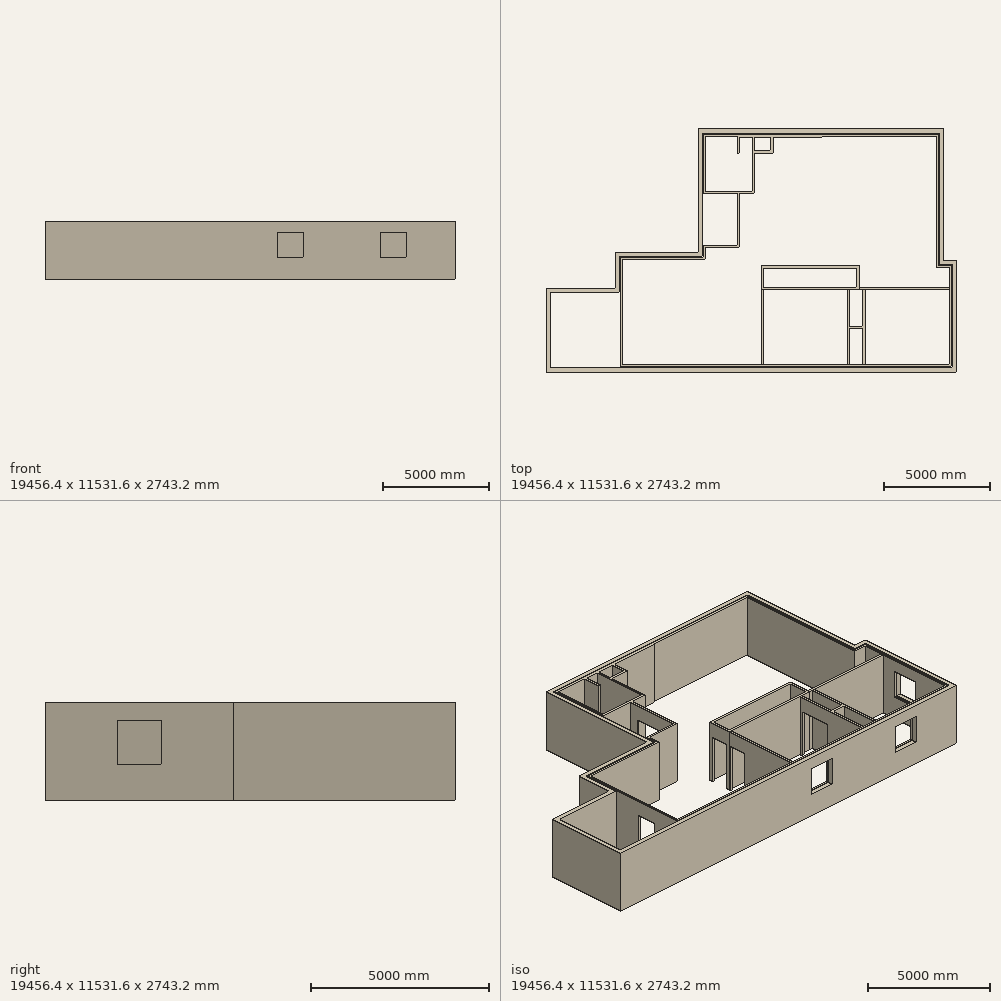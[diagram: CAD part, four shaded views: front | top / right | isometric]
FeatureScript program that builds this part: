
annotation { "Feature Type Name" : "Feature", "Feature Type Description" : "" }
export const myFeature = defineFeature(function(context is Context, id is Id, definition is map)
    precondition{}
    {
        {
            var Q0;
            Q0=qCreatedBy(makeId("Top.planeOp"),FACE);
            var sketch = newSketch(context, id + "F0", { "sketchPlane" : qUnion([Q0])});
            skLineSegment(sketch, "E0.bottom", {"start": v(0, 0) * mm, "end": v(19050, 0) * mm});
            skLineSegment(sketch, "E0.top", {"start": v(7213.6, 11125.2) * mm, "end": v(18440.4, 11125.2) * mm});
            skLineSegment(sketch, "E0.left", {"start": v(0, 0) * mm, "end": v(0, 3556) * mm});
            skLineSegment(sketch, "E0.right", {"start": v(19050, 0) * mm, "end": v(19050, 4876.8) * mm});
            skLineSegment(sketch, "E1", {"start": v(18440.4, 11125.2) * mm, "end": v(18440.4, 4876.8) * mm});
            skLineSegment(sketch, "E2", {"start": v(18440.4, 4876.8) * mm, "end": v(19050, 4876.8) * mm});
            skLineSegment(sketch, "E3", {"start": v(7213.6, 11125.2) * mm, "end": v(7213.6, 5283.2) * mm});
            skLineSegment(sketch, "E4", {"start": v(7213.6, 5283.2) * mm, "end": v(3276.6, 5283.2) * mm});
            skLineSegment(sketch, "E5", {"start": v(3276.6, 5283.2) * mm, "end": v(3276.6, 3556) * mm});
            skLineSegment(sketch, "E6", {"start": v(3276.6, 3556) * mm, "end": v(0, 3556) * mm});
            skLineSegment(sketch, "E7.bottom", {"start": v(9994.9, 4826) * mm, "end": v(14630.4, 4826) * mm, "construction": true});
            skLineSegment(sketch, "E7.top", {"start": v(9994.9, 3708.4) * mm, "end": v(14630.4, 3708.4) * mm, "construction": true});
            skLineSegment(sketch, "E7.left", {"start": v(9994.9, 4826) * mm, "end": v(9994.9, 3708.4) * mm, "construction": true});
            skLineSegment(sketch, "E7.right", {"start": v(14630.4, 4826) * mm, "end": v(14630.4, 3708.4) * mm, "construction": true});
            skPoint(sketch, "E8", {"position": v(16916.4, 0) * mm});
            skPoint(sketch, "E9", {"position": v(15697.2, 0) * mm});
            skPoint(sketch, "E10", {"position": v(12039.6, 0) * mm});
            skPoint(sketch, "E11", {"position": v(10820.4, 0) * mm});
            skPoint(sketch, "E12", {"position": v(12039.6, 11125.2) * mm});
            skPoint(sketch, "E13", {"position": v(10820.4, 11125.2) * mm});
            skPoint(sketch, "E14", {"position": v(19050, 1828.8) * mm});
            skPoint(sketch, "E15", {"position": v(19050, 3048) * mm});
            skLineSegment(sketch, "E16.0", {"start": v(7010.4, 11328.4) * mm, "end": v(18643.6, 11328.4) * mm});
            skLineSegment(sketch, "E17.0", {"start": v(18643.6, 11328.4) * mm, "end": v(18643.6, 5080) * mm});
            skLineSegment(sketch, "E18.0", {"start": v(18643.6, 5080) * mm, "end": v(19253.2, 5080) * mm});
            skLineSegment(sketch, "E19.0", {"start": v(19253.2, -203.2) * mm, "end": v(19253.2, 5080) * mm});
            skLineSegment(sketch, "E20.0", {"start": v(-203.2, -203.2) * mm, "end": v(19253.2, -203.2) * mm});
            skLineSegment(sketch, "E21.0", {"start": v(-203.2, -203.2) * mm, "end": v(-203.2, 3759.2) * mm});
            skLineSegment(sketch, "E22.0", {"start": v(3073.4, 3759.2) * mm, "end": v(-203.2, 3759.2) * mm});
            skLineSegment(sketch, "E23.0", {"start": v(3073.4, 5486.4) * mm, "end": v(3073.4, 3759.2) * mm});
            skLineSegment(sketch, "E24.0", {"start": v(7010.4, 5486.4) * mm, "end": v(3073.4, 5486.4) * mm});
            skLineSegment(sketch, "E25.0", {"start": v(7010.4, 11328.4) * mm, "end": v(7010.4, 5486.4) * mm});
            skPoint(sketch, "E26", {"position": v(8585.2, 11010.9) * mm});
            skPoint(sketch, "E27", {"position": v(9309.1, 10909.3) * mm});
            skPoint(sketch, "E28", {"position": v(8534.4, 10604.5) * mm});
            skSolve(sketch);
        }
        {
            var Q0;
            Q0=qCreatedBy(makeId("Top.planeOp"),FACE);
            var sketch = newSketch(context, id + "F1", { "sketchPlane" : qUnion([Q0])});
            skLineSegment(sketch, "E29", {"start": v(10972.8, 12242.8) * mm, "end": v(10795, 11328.4) * mm});
            skLineSegment(sketch, "E30", {"start": v(10795, 11328.4) * mm, "end": v(12065, 11328.4) * mm});
            skLineSegment(sketch, "E31", {"start": v(12065, 11328.4) * mm, "end": v(11887.2, 12242.8) * mm});
            skLineSegment(sketch, "E32", {"start": v(11887.2, 12242.8) * mm, "end": v(10972.8, 12242.8) * mm});
            skLineSegment(sketch, "E33", {"start": v(10820.4, 11125.2) * mm, "end": v(12039.6, 11125.2) * mm, "construction": true});
            skLineSegment(sketch, "E34", {"start": v(11430, 12242.8) * mm, "end": v(11430, 11125.2) * mm, "construction": true});
            skLineSegment(sketch, "E35", {"start": v(19050, 1828.8) * mm, "end": v(19050, 3048) * mm, "construction": true});
            skLineSegment(sketch, "E36", {"start": v(19253.2, 3073.4) * mm, "end": v(19253.2, 1803.4) * mm});
            skLineSegment(sketch, "E37", {"start": v(19253.2, 1803.4) * mm, "end": v(20167.6, 1981.2) * mm});
            skLineSegment(sketch, "E38", {"start": v(20167.6, 1981.2) * mm, "end": v(20167.6, 2895.6) * mm});
            skLineSegment(sketch, "E39", {"start": v(20167.6, 2895.6) * mm, "end": v(19253.2, 3073.4) * mm});
            skLineSegment(sketch, "E40", {"start": v(19050, 2438.4) * mm, "end": v(19253.2, 2438.4) * mm, "construction": true});
            skLineSegment(sketch, "E41", {"start": v(15697.2, 0) * mm, "end": v(16916.4, 0) * mm, "construction": true});
            skLineSegment(sketch, "E42", {"start": v(16306.8, 0) * mm, "end": v(16306.8, -203.2) * mm, "construction": true});
            skLineSegment(sketch, "E43", {"start": v(15671.8, -203.2) * mm, "end": v(16941.8, -203.2) * mm});
            skLineSegment(sketch, "E44", {"start": v(16941.8, -203.2) * mm, "end": v(16764, -1117.6) * mm});
            skLineSegment(sketch, "E45", {"start": v(16764, -1117.6) * mm, "end": v(15849.6, -1117.6) * mm});
            skLineSegment(sketch, "E46", {"start": v(15849.6, -1117.6) * mm, "end": v(15671.8, -203.2) * mm});
            skLineSegment(sketch, "E47", {"start": v(10820.4, 0) * mm, "end": v(12039.6, 0) * mm, "construction": true});
            skLineSegment(sketch, "E48", {"start": v(10795, -203.2) * mm, "end": v(10972.8, -1117.6) * mm});
            skLineSegment(sketch, "E49", {"start": v(10972.8, -1117.6) * mm, "end": v(11887.2, -1117.6) * mm});
            skLineSegment(sketch, "E50", {"start": v(11887.2, -1117.6) * mm, "end": v(12065, -203.2) * mm});
            skLineSegment(sketch, "E51", {"start": v(12065, -203.2) * mm, "end": v(10795, -203.2) * mm});
            skLineSegment(sketch, "E52", {"start": v(11430, 0) * mm, "end": v(11430, -203.2) * mm, "construction": true});
            skSolve(sketch);
        }
        {
            var Q0;
            Q0=makeQuery(id+"F0.imprint","IMPRINT",FACE,{"disambiguationData":[TD([[makeQuery(id+"F0.imprint","IMPRINT",EDGE,{"derivedFrom":sQuery(id+"F0.wireOp",EDGE,"E0.bottom")}),-1.0]])]});
            extrude(context, id + "F2", {"entities" : qUnion([Q0]), "depth" : 2743.2 * mm});
        }
        {
            var Q0;
            Q0=qCreatedBy(makeId("Top.planeOp"),FACE);
            var sketch = newSketch(context, id + "F3", { "sketchPlane" : qUnion([Q0])});
            skLineSegment(sketch, "E53.bottom", {"start": v(10096.5, 4724.4) * mm, "end": v(14528.8, 4724.4) * mm});
            skLineSegment(sketch, "E53.top", {"start": v(10096.5, 3810) * mm, "end": v(14528.8, 3810) * mm});
            skLineSegment(sketch, "E53.left", {"start": v(10096.5, 4724.4) * mm, "end": v(10096.5, 3810) * mm});
            skLineSegment(sketch, "E53.right", {"start": v(14528.8, 4724.4) * mm, "end": v(14528.8, 3810) * mm});
            skLineSegment(sketch, "E54.bottom", {"start": v(9982.2, 4838.7) * mm, "end": v(14643.1, 4838.7) * mm});
            skLineSegment(sketch, "E54.top", {"start": v(9982.2, 3695.7) * mm, "end": v(14643.1, 3695.7) * mm});
            skLineSegment(sketch, "E54.left", {"start": v(9982.2, 4838.7) * mm, "end": v(9982.2, 3695.7) * mm});
            skLineSegment(sketch, "E54.right", {"start": v(14643.1, 4838.7) * mm, "end": v(14643.1, 3695.7) * mm});
            skSolve(sketch);
        }
        {
            var Q0;
            Q0 = qSketchRegion(id + "F3", true);
            extrude(context, id + "F4", {"entities" : qUnion([Q0]), "depth" : 2743.2 * mm});
        }
        {
            var Q0;
            Q0=qCreatedBy(makeId("Top.planeOp"),FACE);
            var sketch = newSketch(context, id + "F5", { "sketchPlane" : qUnion([Q0])});
            skLineSegment(sketch, "E55", {"start": v(3314.7, 5245.1) * mm, "end": v(3314.7, 38.1) * mm});
            skLineSegment(sketch, "E56", {"start": v(3314.7, 38.1) * mm, "end": v(19011.9, 38.1) * mm});
            skLineSegment(sketch, "E57", {"start": v(19011.9, 38.1) * mm, "end": v(19011.9, 4838.7) * mm});
            skLineSegment(sketch, "E58", {"start": v(19011.9, 4838.7) * mm, "end": v(18402.3, 4838.7) * mm});
            skLineSegment(sketch, "E59", {"start": v(18402.3, 4838.7) * mm, "end": v(18402.3, 11087.1) * mm});
            skLineSegment(sketch, "E60", {"start": v(18402.3, 11087.1) * mm, "end": v(7251.7, 11087.1) * mm});
            skLineSegment(sketch, "E61", {"start": v(7251.7, 11087.1) * mm, "end": v(7251.7, 8280.4) * mm});
            skLineSegment(sketch, "E62", {"start": v(7251.7, 8280.4) * mm, "end": v(8839.2, 8280.4) * mm});
            skLineSegment(sketch, "E63", {"start": v(8839.2, 8280.4) * mm, "end": v(8839.2, 5791.2) * mm});
            skLineSegment(sketch, "E64", {"start": v(8839.2, 5791.2) * mm, "end": v(7251.7, 5791.2) * mm});
            skLineSegment(sketch, "E65", {"start": v(7251.7, 5791.2) * mm, "end": v(7251.7, 5245.1) * mm});
            skLineSegment(sketch, "E66", {"start": v(7251.7, 5245.1) * mm, "end": v(3314.7, 5245.1) * mm});
            skLineSegment(sketch, "E67.0", {"start": v(18300.7, 10985.5) * mm, "end": v(7353.3, 10985.5) * mm});
            skLineSegment(sketch, "E67.1", {"start": v(7353.3, 5689.6) * mm, "end": v(7353.3, 5143.5) * mm});
            skLineSegment(sketch, "E67.2", {"start": v(8940.8, 5689.6) * mm, "end": v(7353.3, 5689.6) * mm});
            skLineSegment(sketch, "E67.3", {"start": v(8940.8, 8382) * mm, "end": v(8940.8, 5689.6) * mm});
            skLineSegment(sketch, "E67.4", {"start": v(7353.3, 8382) * mm, "end": v(8940.8, 8382) * mm});
            skLineSegment(sketch, "E67.5", {"start": v(7353.3, 5143.5) * mm, "end": v(3416.3, 5143.5) * mm});
            skLineSegment(sketch, "E67.6", {"start": v(7353.3, 10985.5) * mm, "end": v(7353.3, 8382) * mm});
            skLineSegment(sketch, "E67.7", {"start": v(3416.3, 5143.5) * mm, "end": v(3416.3, 139.7) * mm});
            skLineSegment(sketch, "E67.8", {"start": v(3416.3, 139.7) * mm, "end": v(18910.3, 139.7) * mm});
            skLineSegment(sketch, "E67.9", {"start": v(18910.3, 139.7) * mm, "end": v(18910.3, 4737.1) * mm});
            skLineSegment(sketch, "E67.10", {"start": v(18910.3, 4737.1) * mm, "end": v(18300.7, 4737.1) * mm});
            skLineSegment(sketch, "E67.11", {"start": v(18300.7, 4737.1) * mm, "end": v(18300.7, 10985.5) * mm});
            skSolve(sketch);
        }
        {
            var Q0;
            Q0 = qSketchRegion(id + "F5", true);
            extrude(context, id + "F6", {"entities" : qUnion([Q0]), "depth" : 2743.2 * mm});
        }
        {
            var Q0;
            Q0=qCreatedBy(makeId("Top.planeOp"),FACE);
            var sketch = newSketch(context, id + "F7", { "sketchPlane" : qUnion([Q0])});
            skLineSegment(sketch, "E68", {"start": v(8940.8, 8382) * mm, "end": v(9569.45, 8382) * mm});
            skLineSegment(sketch, "E69", {"start": v(9569.45, 8382) * mm, "end": v(9569.45, 10934.7) * mm});
            skLineSegment(sketch, "E70", {"start": v(9683.75, 10934.7) * mm, "end": v(9683.75, 10299.7) * mm});
            skLineSegment(sketch, "E71", {"start": v(9683.75, 8280.4) * mm, "end": v(8940.8, 8280.4) * mm});
            skLineSegment(sketch, "E72", {"start": v(8940.8, 8280.4) * mm, "end": v(8940.8, 8382) * mm});
            skLineSegment(sketch, "E73.bottom", {"start": v(8845.55, 10934.7) * mm, "end": v(8959.85, 10934.7) * mm});
            skLineSegment(sketch, "E73.top", {"start": v(8845.55, 10172.7) * mm, "end": v(8959.85, 10172.7) * mm});
            skLineSegment(sketch, "E73.left", {"start": v(8845.55, 10934.7) * mm, "end": v(8845.55, 10172.7) * mm});
            skLineSegment(sketch, "E73.right", {"start": v(8959.85, 10934.7) * mm, "end": v(8959.85, 10172.7) * mm});
            skLineSegment(sketch, "E74", {"start": v(10560.05, 10934.7) * mm, "end": v(10560.05, 10185.4) * mm});
            skLineSegment(sketch, "E75", {"start": v(10560.05, 10185.4) * mm, "end": v(9683.75, 10185.4) * mm});
            skLineSegment(sketch, "E76", {"start": v(9683.75, 10299.7) * mm, "end": v(10445.75, 10299.7) * mm});
            skLineSegment(sketch, "E77", {"start": v(10445.75, 10299.7) * mm, "end": v(10445.75, 10934.7) * mm});
            skLineSegment(sketch, "E78.bottom", {"start": v(8845.55, 10985.5) * mm, "end": v(12903.2, 10985.5) * mm});
            skLineSegment(sketch, "E78.top", {"start": v(8845.55, 10934.7) * mm, "end": v(9569.45, 10934.7) * mm});
            skLineSegment(sketch, "E78.left", {"start": v(8845.55, 10985.5) * mm, "end": v(8845.55, 10934.7) * mm});
            skLineSegment(sketch, "E78.right", {"start": v(12903.2, 10985.5) * mm, "end": v(12903.2, 10934.7) * mm});
            skLineSegment(sketch, "E79.trimOffspring", {"start": v(9683.75, 10185.4) * mm, "end": v(9683.75, 8280.4) * mm});
            skLineSegment(sketch, "E80.trimOffspring", {"start": v(10560.05, 10934.7) * mm, "end": v(12903.2, 10934.7) * mm});
            skLineSegment(sketch, "E81.trimOffspring", {"start": v(9683.75, 10934.7) * mm, "end": v(10445.75, 10934.7) * mm});
            skPoint(sketch, "E82", {"position": v(10972.8, 10934.7) * mm});
            skPoint(sketch, "E83", {"position": v(11887.2, 10934.7) * mm});
            skPoint(sketch, "E84", {"position": v(12496.8, 10934.7) * mm});
            skLineSegment(sketch, "E85.bottom", {"start": v(10560.05, 10934.7) * mm, "end": v(10972.8, 10934.7) * mm, "construction": true});
            skLineSegment(sketch, "E85.top", {"start": v(10560.05, 10325.1) * mm, "end": v(10972.8, 10325.1) * mm, "construction": true});
            skLineSegment(sketch, "E85.left", {"start": v(10560.05, 10934.7) * mm, "end": v(10560.05, 10325.1) * mm, "construction": true});
            skLineSegment(sketch, "E85.right", {"start": v(10972.8, 10934.7) * mm, "end": v(10972.8, 10325.1) * mm, "construction": true});
            skLineSegment(sketch, "E86.bottom", {"start": v(10972.8, 10934.7) * mm, "end": v(11887.2, 10934.7) * mm, "construction": true});
            skLineSegment(sketch, "E86.top", {"start": v(10972.8, 10325.1) * mm, "end": v(11887.2, 10325.1) * mm, "construction": true});
            skLineSegment(sketch, "E86.right", {"start": v(11887.2, 10934.7) * mm, "end": v(11887.2, 10325.1) * mm, "construction": true});
            skLineSegment(sketch, "E87.bottom", {"start": v(11887.2, 10934.7) * mm, "end": v(12496.8, 10934.7) * mm, "construction": true});
            skLineSegment(sketch, "E87.top", {"start": v(11887.2, 10325.1) * mm, "end": v(12496.8, 10325.1) * mm, "construction": true});
            skLineSegment(sketch, "E87.right", {"start": v(12496.8, 10934.7) * mm, "end": v(12496.8, 10325.1) * mm, "construction": true});
            skLineSegment(sketch, "E88.bottom", {"start": v(12496.8, 10934.7) * mm, "end": v(12903.2, 10934.7) * mm, "construction": true});
            skLineSegment(sketch, "E88.top", {"start": v(12496.8, 10325.1) * mm, "end": v(12903.2, 10325.1) * mm, "construction": true});
            skLineSegment(sketch, "E88.right", {"start": v(12903.2, 10934.7) * mm, "end": v(12903.2, 10325.1) * mm, "construction": true});
            skPoint(sketch, "E89", {"position": v(11430, 10325.1) * mm});
            skSolve(sketch);
        }
        {
            var Q0;
            Q0 = qSketchRegion(id + "F7", true);
            var Q1;
            Q1=makeQuery(id+"F2.opExtrude","CAP_FACE",FACE,{"disambiguationData":[OSD([sQuery(id+"F0.wireOp",EDGE,"E0.bottom"),sQuery(id+"F0.wireOp",EDGE,"E0.top"),sQuery(id+"F0.wireOp",EDGE,"E0.left"),sQuery(id+"F0.wireOp",EDGE,"E0.right"),sQuery(id+"F0.wireOp",EDGE,"E1"),sQuery(id+"F0.wireOp",EDGE,"E2"),sQuery(id+"F0.wireOp",EDGE,"E3"),sQuery(id+"F0.wireOp",EDGE,"E4"),sQuery(id+"F0.wireOp",EDGE,"E5"),sQuery(id+"F0.wireOp",EDGE,"E6"),sQuery(id+"F0.wireOp",EDGE,"E16.0"),sQuery(id+"F0.wireOp",EDGE,"E17.0"),sQuery(id+"F0.wireOp",EDGE,"E18.0"),sQuery(id+"F0.wireOp",EDGE,"E19.0"),sQuery(id+"F0.wireOp",EDGE,"E20.0"),sQuery(id+"F0.wireOp",EDGE,"E21.0"),sQuery(id+"F0.wireOp",EDGE,"E22.0"),sQuery(id+"F0.wireOp",EDGE,"E23.0"),sQuery(id+"F0.wireOp",EDGE,"E24.0"),sQuery(id+"F0.wireOp",EDGE,"E25.0")])],"isStart":false});
            extrude(context, id + "F8", {"entities" : qUnion([Q0]), "operationType" : NewBodyOperationType.ADD, "endBound" : BoundingType.UP_TO_SURFACE, "endBoundEntityFace" : qUnion([Q1]), "depth" : 25.4 * mm});
        }
        {
            var Q0;
            Q0=qCreatedBy(makeId("Top.planeOp"),FACE);
            var sketch = newSketch(context, id + "F9", { "sketchPlane" : qUnion([Q0])});
            skLineSegment(sketch, "E90.bottom", {"start": v(9982.2, 3695.7) * mm, "end": v(10096.5, 3695.7) * mm});
            skLineSegment(sketch, "E90.top", {"start": v(9982.2, 139.7) * mm, "end": v(10096.5, 139.7) * mm});
            skLineSegment(sketch, "E90.left", {"start": v(9982.2, 3695.7) * mm, "end": v(9982.2, 139.7) * mm});
            skLineSegment(sketch, "E90.right", {"start": v(10096.5, 3695.7) * mm, "end": v(10096.5, 139.7) * mm});
            skLineSegment(sketch, "E91.bottom", {"start": v(14643.1, 3695.7) * mm, "end": v(18910.3, 3695.7) * mm});
            skLineSegment(sketch, "E91.top", {"start": v(14643.1, 3810) * mm, "end": v(18910.3, 3810) * mm});
            skLineSegment(sketch, "E91.left", {"start": v(14643.1, 3695.7) * mm, "end": v(14643.1, 3810) * mm});
            skLineSegment(sketch, "E91.right", {"start": v(18910.3, 3695.7) * mm, "end": v(18910.3, 3810) * mm});
            skSolve(sketch);
        }
        {
            var Q0;
            Q0 = qSketchRegion(id + "F9", true);
            extrude(context, id + "F10", {"entities" : qUnion([Q0]), "depth" : 2743.2 * mm});
        }
        {
            var Q0;
            Q0=makeQuery(id+"F2.opExtrude","SWEPT_FACE",FACE,{"disambiguationData":[OSD([sQuery(id+"F0.wireOp",EDGE,"E20.0")])]});
            var sketch = newSketch(context, id + "F11", { "sketchPlane" : qUnion([Q0])});
            skLineSegment(sketch, "E92.bottom", {"start": v(10820.4, 1016) * mm, "end": v(12039.6, 1016) * mm});
            skLineSegment(sketch, "E92.top", {"start": v(10820.4, 2235.2) * mm, "end": v(12039.6, 2235.2) * mm});
            skLineSegment(sketch, "E92.left", {"start": v(10820.4, 1016) * mm, "end": v(10820.4, 2235.2) * mm});
            skLineSegment(sketch, "E92.right", {"start": v(12039.6, 1016) * mm, "end": v(12039.6, 2235.2) * mm});
            skLineSegment(sketch, "E93.bottom", {"start": v(15697.2, 1016) * mm, "end": v(16916.4, 1016) * mm});
            skLineSegment(sketch, "E93.top", {"start": v(15697.2, 2235.2) * mm, "end": v(16916.4, 2235.2) * mm});
            skLineSegment(sketch, "E93.left", {"start": v(15697.2, 1016) * mm, "end": v(15697.2, 2235.2) * mm});
            skLineSegment(sketch, "E93.right", {"start": v(16916.4, 1016) * mm, "end": v(16916.4, 2235.2) * mm});
            skSolve(sketch);
        }
        {
            var Q0;
            Q0 = qSketchRegion(id + "F11", true);
            var Q1;
            Q1=makeQuery(id+"F6.opExtrude","SWEPT_FACE",FACE,{"disambiguationData":[OSD([sQuery(id+"F5.wireOp",EDGE,"E67.8")])]});
            extrude(context, id + "F12", {"entities" : qUnion([Q0]), "operationType" : NewBodyOperationType.REMOVE, "endBound" : BoundingType.UP_TO_SURFACE, "oppositeDirection" : true, "endBoundEntityFace" : qUnion([Q1]), "depth" : 25.4 * mm});
        }
        {
            var Q0;
            Q0=qCreatedBy(makeId("Top.planeOp"),FACE);
            var sketch = newSketch(context, id + "F13", { "sketchPlane" : qUnion([Q0])});
            skLineSegment(sketch, "E94", {"start": v(10096.5, 1917.7) * mm, "end": v(14503.4, 1917.7) * mm, "construction": true});
            skLineSegment(sketch, "E95", {"start": v(14503.4, 1917.7) * mm, "end": v(18910.3, 1917.7) * mm, "construction": true});
            skLineSegment(sketch, "E96", {"start": v(14503.4, 3695.7) * mm, "end": v(14503.4, 139.7) * mm, "construction": true});
            skLineSegment(sketch, "E97.bottom", {"start": v(14084.3, 3695.7) * mm, "end": v(14198.6, 3695.7) * mm});
            skLineSegment(sketch, "E97.top", {"start": v(14084.3, 139.7) * mm, "end": v(14198.6, 139.7) * mm});
            skLineSegment(sketch, "E97.left", {"start": v(14084.3, 3695.7) * mm, "end": v(14084.3, 139.7) * mm});
            skLineSegment(sketch, "E97.right", {"start": v(14198.6, 3695.7) * mm, "end": v(14198.6, 1974.85) * mm});
            skLineSegment(sketch, "E98.bottom", {"start": v(14808.2, 3695.7) * mm, "end": v(14922.5, 3695.7) * mm});
            skLineSegment(sketch, "E98.top", {"start": v(14808.2, 139.7) * mm, "end": v(14922.5, 139.7) * mm});
            skLineSegment(sketch, "E98.left", {"start": v(14808.2, 3695.7) * mm, "end": v(14808.2, 1974.85) * mm});
            skLineSegment(sketch, "E98.right", {"start": v(14922.5, 3695.7) * mm, "end": v(14922.5, 139.7) * mm});
            skLineSegment(sketch, "E99.bottom", {"start": v(14198.6, 1974.85) * mm, "end": v(14808.2, 1974.85) * mm});
            skLineSegment(sketch, "E99.top", {"start": v(14198.6, 1860.55) * mm, "end": v(14808.2, 1860.55) * mm});
            skPoint(sketch, "E100", {"position": v(14503.4, 1974.85) * mm});
            skLineSegment(sketch, "E101.trimOffspring", {"start": v(14808.2, 1860.55) * mm, "end": v(14808.2, 139.7) * mm});
            skLineSegment(sketch, "E102", {"start": v(14198.6, 1860.55) * mm, "end": v(14198.6, 139.7) * mm});
            skSolve(sketch);
        }
        {
            var Q0;
            Q0 = qSketchRegion(id + "F13", true);
            var Q1;
            Q1=makeQuery(id+"F2.opExtrude","CAP_FACE",FACE,{"disambiguationData":[OSD([sQuery(id+"F0.wireOp",EDGE,"E0.bottom"),sQuery(id+"F0.wireOp",EDGE,"E0.top"),sQuery(id+"F0.wireOp",EDGE,"E0.left"),sQuery(id+"F0.wireOp",EDGE,"E0.right"),sQuery(id+"F0.wireOp",EDGE,"E1"),sQuery(id+"F0.wireOp",EDGE,"E2"),sQuery(id+"F0.wireOp",EDGE,"E3"),sQuery(id+"F0.wireOp",EDGE,"E4"),sQuery(id+"F0.wireOp",EDGE,"E5"),sQuery(id+"F0.wireOp",EDGE,"E6"),sQuery(id+"F0.wireOp",EDGE,"E16.0"),sQuery(id+"F0.wireOp",EDGE,"E17.0"),sQuery(id+"F0.wireOp",EDGE,"E18.0"),sQuery(id+"F0.wireOp",EDGE,"E19.0"),sQuery(id+"F0.wireOp",EDGE,"E20.0"),sQuery(id+"F0.wireOp",EDGE,"E21.0"),sQuery(id+"F0.wireOp",EDGE,"E22.0"),sQuery(id+"F0.wireOp",EDGE,"E23.0"),sQuery(id+"F0.wireOp",EDGE,"E24.0"),sQuery(id+"F0.wireOp",EDGE,"E25.0")])],"isStart":false});
            extrude(context, id + "F14", {"entities" : qUnion([Q0]), "endBound" : BoundingType.UP_TO_SURFACE, "endBoundEntityFace" : qUnion([Q1]), "depth" : 25.4 * mm});
        }
        {
            var Q0;
            Q0=makeQuery(id+"F14.opExtrude","SWEPT_FACE",FACE,{"disambiguationData":[OSD([sQuery(id+"F13.wireOp",EDGE,"E98.right")])]});
            var sketch = newSketch(context, id + "F15", { "sketchPlane" : qUnion([Q0])});
            skLineSegment(sketch, "E103.bottom", {"start": v(257.17, 0) * mm, "end": v(1743.07, 0) * mm});
            skLineSegment(sketch, "E103.top", {"start": v(257.17, 2082.8) * mm, "end": v(1743.07, 2082.8) * mm});
            skLineSegment(sketch, "E103.left", {"start": v(257.17, 0) * mm, "end": v(257.17, 2082.8) * mm});
            skLineSegment(sketch, "E103.right", {"start": v(1743.07, 0) * mm, "end": v(1743.07, 2082.8) * mm});
            skLineSegment(sketch, "E104", {"start": v(1743.07, 2082.8) * mm, "end": v(1860.55, 2082.8) * mm, "construction": true});
            skLineSegment(sketch, "E105", {"start": v(257.17, 2082.8) * mm, "end": v(139.7, 2082.8) * mm, "construction": true});
            skSolve(sketch);
        }
        {
            var Q0;
            Q0 = qSketchRegion(id + "F15", true);
            extrude(context, id + "F16", {"entities" : qUnion([Q0]), "operationType" : NewBodyOperationType.REMOVE, "endBound" : BoundingType.UP_TO_NEXT, "oppositeDirection" : true, "depth" : 25.4 * mm});
        }
        {
            var Q0;
            Q0=makeQuery(id+"F14.opExtrude","SWEPT_FACE",FACE,{"disambiguationData":[OSD([sQuery(id+"F13.wireOp",EDGE,"E97.left")])]});
            var sketch = newSketch(context, id + "F17", { "sketchPlane" : qUnion([Q0])});
            skLineSegment(sketch, "E106.bottom", {"start": v(-3578.23, 0) * mm, "end": v(-2092.32, 0) * mm});
            skLineSegment(sketch, "E106.top", {"start": v(-3578.23, 2082.8) * mm, "end": v(-2092.32, 2082.8) * mm});
            skLineSegment(sketch, "E106.left", {"start": v(-3578.23, 0) * mm, "end": v(-3578.23, 2082.8) * mm});
            skLineSegment(sketch, "E106.right", {"start": v(-2092.32, 0) * mm, "end": v(-2092.32, 2082.8) * mm});
            skLineSegment(sketch, "E107", {"start": v(-3578.23, 2082.8) * mm, "end": v(-3695.7, 2082.8) * mm, "construction": true});
            skLineSegment(sketch, "E108", {"start": v(-2092.32, 2082.8) * mm, "end": v(-1974.85, 2082.8) * mm, "construction": true});
            skSolve(sketch);
        }
        {
            var Q0;
            Q0 = qSketchRegion(id + "F17", true);
            extrude(context, id + "F18", {"entities" : qUnion([Q0]), "operationType" : NewBodyOperationType.REMOVE, "endBound" : BoundingType.UP_TO_NEXT, "oppositeDirection" : true, "depth" : 25.4 * mm});
        }
        {
            var Q0;
            Q0=qCreatedBy(makeId("Top.planeOp"),FACE);
            var sketch = newSketch(context, id + "F19", { "sketchPlane" : qUnion([Q0])});
            skArc(sketch, "E109", {"start": v(10096.5, 2844.8) * mm, "mid": v(10635.32, 3067.98) * mm, "end": v(10858.5, 3606.8) * mm, "construction": true});
            skArc(sketch, "E110", {"start": v(9982.2, 3886.2) * mm, "mid": v(9443.38, 4109.38) * mm, "end": v(9220.2, 4648.2) * mm, "construction": true});
            skLineSegment(sketch, "E111", {"start": v(10096.5, 3606.8) * mm, "end": v(10858.5, 3606.8) * mm, "construction": true});
            skLineSegment(sketch, "E112", {"start": v(10096.5, 3606.8) * mm, "end": v(10096.5, 2844.8) * mm, "construction": true});
            skLineSegment(sketch, "E113", {"start": v(9982.2, 3886.2) * mm, "end": v(9982.2, 4648.2) * mm, "construction": true});
            skLineSegment(sketch, "E114", {"start": v(9220.2, 4648.2) * mm, "end": v(9982.2, 4648.2) * mm, "construction": true});
            skLineSegment(sketch, "E115", {"start": v(9982.2, 4648.2) * mm, "end": v(9982.2, 4724.4) * mm, "construction": true});
            skLineSegment(sketch, "E116", {"start": v(9982.2, 3886.2) * mm, "end": v(9982.2, 3810) * mm, "construction": true});
            skArc(sketch, "E117", {"start": v(15836.9, 2933.7) * mm, "mid": v(16375.72, 3156.88) * mm, "end": v(16598.9, 3695.7) * mm, "construction": true});
            skArc(sketch, "E118", {"start": v(8940.8, 6985) * mm, "mid": v(9587.38, 6717.18) * mm, "end": v(9855.2, 6070.6) * mm, "construction": true});
            skArc(sketch, "E119", {"start": v(8940.8, 6985) * mm, "mid": v(9587.38, 7252.82) * mm, "end": v(9855.2, 7899.4) * mm, "construction": true});
            skLineSegment(sketch, "E120", {"start": v(8940.8, 7899.4) * mm, "end": v(9855.2, 7899.4) * mm, "construction": true});
            skLineSegment(sketch, "E121", {"start": v(8940.8, 6985) * mm, "end": v(8940.8, 7899.4) * mm, "construction": true});
            skLineSegment(sketch, "E122", {"start": v(8940.8, 6985) * mm, "end": v(8940.8, 6070.6) * mm, "construction": true});
            skLineSegment(sketch, "E123", {"start": v(8940.8, 6070.6) * mm, "end": v(9855.2, 6070.6) * mm, "construction": true});
            skLineSegment(sketch, "E124", {"start": v(15836.9, 2933.7) * mm, "end": v(15836.9, 3695.7) * mm, "construction": true});
            skLineSegment(sketch, "E125", {"start": v(15836.9, 3695.7) * mm, "end": v(16598.9, 3695.7) * mm, "construction": true});
            skArc(sketch, "E126", {"start": v(3416.3, 2273.3) * mm, "mid": v(4062.88, 2005.48) * mm, "end": v(4330.7, 1358.9) * mm, "construction": true});
            skLineSegment(sketch, "E127", {"start": v(3416.3, 2273.3) * mm, "end": v(3416.3, 1358.9) * mm, "construction": true});
            skLineSegment(sketch, "E128", {"start": v(3416.3, 1358.9) * mm, "end": v(4330.7, 1358.9) * mm, "construction": true});
            skArc(sketch, "E129", {"start": v(14643.1, 4673.6) * mm, "mid": v(15217.84, 4435.54) * mm, "end": v(15455.9, 3860.8) * mm, "construction": true});
            skLineSegment(sketch, "E130", {"start": v(15455.9, 3860.8) * mm, "end": v(14643.1, 3860.8) * mm, "construction": true});
            skLineSegment(sketch, "E131", {"start": v(14643.1, 3860.8) * mm, "end": v(14643.1, 4673.6) * mm, "construction": true});
            skLineSegment(sketch, "E132", {"start": v(14643.1, 4673.6) * mm, "end": v(14643.1, 4724.4) * mm, "construction": true});
            skLineSegment(sketch, "E133", {"start": v(14643.1, 3860.8) * mm, "end": v(14643.1, 3810) * mm, "construction": true});
            skArc(sketch, "E134", {"start": v(9569.45, 9220.2) * mm, "mid": v(9030.63, 8997.02) * mm, "end": v(8807.45, 8458.2) * mm, "construction": true});
            skLineSegment(sketch, "E135", {"start": v(8807.45, 8458.2) * mm, "end": v(9569.45, 8458.2) * mm, "construction": true});
            skLineSegment(sketch, "E136", {"start": v(9569.45, 8458.2) * mm, "end": v(9569.45, 9220.2) * mm, "construction": true});
            skArc(sketch, "E137", {"start": v(9759.95, 9575.8) * mm, "mid": v(10191, 9754.35) * mm, "end": v(10369.55, 10185.4) * mm, "construction": true});
            skLineSegment(sketch, "E138", {"start": v(9759.95, 9575.8) * mm, "end": v(9759.95, 10185.4) * mm, "construction": true});
            skLineSegment(sketch, "E139", {"start": v(9759.95, 10185.4) * mm, "end": v(10369.55, 10185.4) * mm, "construction": true});
            skSolve(sketch);
        }
        {
            var Q0;
            Q0=makeQuery(id+"F10.opExtrude","SWEPT_FACE",FACE,{"disambiguationData":[OSD([sQuery(id+"F9.wireOp",EDGE,"E90.left")])]});
            var sketch = newSketch(context, id + "F20", { "sketchPlane" : qUnion([Q0])});
            skLineSegment(sketch, "E140.bottom", {"start": v(-3606.8, 0) * mm, "end": v(-2844.8, 0) * mm});
            skLineSegment(sketch, "E140.top", {"start": v(-3606.8, 2082.8) * mm, "end": v(-2844.8, 2082.8) * mm});
            skLineSegment(sketch, "E140.left", {"start": v(-3606.8, 0) * mm, "end": v(-3606.8, 2082.8) * mm});
            skLineSegment(sketch, "E140.right", {"start": v(-2844.8, 0) * mm, "end": v(-2844.8, 2082.8) * mm});
            skSolve(sketch);
        }
        {
            var Q0;
            Q0 = qSketchRegion(id + "F20", true);
            extrude(context, id + "F21", {"entities" : qUnion([Q0]), "operationType" : NewBodyOperationType.REMOVE, "endBound" : BoundingType.UP_TO_NEXT, "oppositeDirection" : true, "depth" : 25.4 * mm});
        }
        {
            var Q0;
            Q0=makeQuery(id+"F4.opExtrude","SWEPT_FACE",FACE,{"disambiguationData":[OSD([sQuery(id+"F3.wireOp",EDGE,"E54.left")])]});
            var sketch = newSketch(context, id + "F22", { "sketchPlane" : qUnion([Q0])});
            skLineSegment(sketch, "E141.bottom", {"start": v(-4648.2, 0) * mm, "end": v(-3886.2, 0) * mm});
            skLineSegment(sketch, "E141.top", {"start": v(-4648.2, 2082.8) * mm, "end": v(-3886.2, 2082.8) * mm});
            skLineSegment(sketch, "E141.left", {"start": v(-4648.2, 0) * mm, "end": v(-4648.2, 2082.8) * mm});
            skLineSegment(sketch, "E141.right", {"start": v(-3886.2, 0) * mm, "end": v(-3886.2, 2082.8) * mm});
            skSolve(sketch);
        }
        {
            var Q0;
            Q0 = qSketchRegion(id + "F22", true);
            var Q1;
            Q1=makeQuery(id+"F4.opExtrude","SWEPT_FACE",FACE,{"disambiguationData":[OSD([sQuery(id+"F3.wireOp",EDGE,"E54.right")])]});
            extrude(context, id + "F23", {"entities" : qUnion([Q0]), "operationType" : NewBodyOperationType.REMOVE, "endBound" : BoundingType.UP_TO_SURFACE, "oppositeDirection" : true, "endBoundEntityFace" : qUnion([Q1]), "depth" : 25.4 * mm});
        }
        {
            var Q0;
            Q0=makeQuery(id+"F6.opExtrude","SWEPT_FACE",FACE,{"disambiguationData":[OSD([sQuery(id+"F5.wireOp",EDGE,"E67.3")])]});
            var sketch = newSketch(context, id + "F24", { "sketchPlane" : qUnion([Q0])});
            skLineSegment(sketch, "E142.bottom", {"start": v(6070.6, 0) * mm, "end": v(7899.4, 0) * mm});
            skLineSegment(sketch, "E142.top", {"start": v(6070.6, 2082.8) * mm, "end": v(7899.4, 2082.8) * mm});
            skLineSegment(sketch, "E142.left", {"start": v(6070.6, 0) * mm, "end": v(6070.6, 2082.8) * mm});
            skLineSegment(sketch, "E142.right", {"start": v(7899.4, 0) * mm, "end": v(7899.4, 2082.8) * mm});
            skSolve(sketch);
        }
        {
            var Q0;
            Q0 = qSketchRegion(id + "F24", true);
            extrude(context, id + "F25", {"entities" : qUnion([Q0]), "operationType" : NewBodyOperationType.REMOVE, "endBound" : BoundingType.UP_TO_NEXT, "oppositeDirection" : true, "depth" : 25.4 * mm});
        }
        {
            var Q0;
            Q0=makeQuery(id+"F6.opExtrude","SWEPT_FACE",FACE,{"disambiguationData":[OSD([sQuery(id+"F5.wireOp",EDGE,"E67.7")])]});
            var sketch = newSketch(context, id + "F26", { "sketchPlane" : qUnion([Q0])});
            skLineSegment(sketch, "E143.bottom", {"start": v(1358.9, 0) * mm, "end": v(2273.3, 0) * mm});
            skLineSegment(sketch, "E143.top", {"start": v(1358.9, 2082.8) * mm, "end": v(2273.3, 2082.8) * mm});
            skLineSegment(sketch, "E143.left", {"start": v(1358.9, 0) * mm, "end": v(1358.9, 2082.8) * mm});
            skLineSegment(sketch, "E143.right", {"start": v(2273.3, 0) * mm, "end": v(2273.3, 2082.8) * mm});
            skSolve(sketch);
        }
        {
            var Q0;
            Q0 = qSketchRegion(id + "F26", true);
            extrude(context, id + "F27", {"entities" : qUnion([Q0]), "operationType" : NewBodyOperationType.REMOVE, "endBound" : BoundingType.UP_TO_NEXT, "oppositeDirection" : true, "depth" : 25.4 * mm});
        }
        {
            var Q0;
            Q0=makeQuery(id+"F2.opExtrude","SWEPT_FACE",FACE,{"disambiguationData":[OSD([sQuery(id+"F0.wireOp",EDGE,"E19.0")])]});
            var sketch = newSketch(context, id + "F28", { "sketchPlane" : qUnion([Q0])});
            skLineSegment(sketch, "E144.bottom", {"start": v(1828.8, 2235.2) * mm, "end": v(3048, 2235.2) * mm});
            skLineSegment(sketch, "E144.top", {"start": v(1828.8, 1016) * mm, "end": v(3048, 1016) * mm});
            skLineSegment(sketch, "E144.left", {"start": v(1828.8, 2235.2) * mm, "end": v(1828.8, 1016) * mm});
            skLineSegment(sketch, "E144.right", {"start": v(3048, 2235.2) * mm, "end": v(3048, 1016) * mm});
            skSolve(sketch);
        }
        {
            var Q0;
            Q0 = qSketchRegion(id + "F28", true);
            var Q1;
            Q1=makeQuery(id+"F6.opExtrude","SWEPT_FACE",FACE,{"disambiguationData":[OSD([sQuery(id+"F5.wireOp",EDGE,"E67.9")])]});
            extrude(context, id + "F29", {"entities" : qUnion([Q0]), "operationType" : NewBodyOperationType.REMOVE, "endBound" : BoundingType.UP_TO_SURFACE, "oppositeDirection" : true, "endBoundEntityFace" : qUnion([Q1]), "depth" : 25.4 * mm});
        }
        {
            var Q0;
            Q0=makeQuery(id+"F2.opExtrude","SWEPT_FACE",FACE,{"disambiguationData":[OSD([sQuery(id+"F0.wireOp",EDGE,"E16.0")])]});
            var sketch = newSketch(context, id + "F30", { "sketchPlane" : qUnion([Q0])});
            skLineSegment(sketch, "E145.bottom", {"start": v(-12039.6, 1016) * mm, "end": v(-10820.4, 1016) * mm});
            skLineSegment(sketch, "E145.top", {"start": v(-12039.6, 2235.2) * mm, "end": v(-10820.4, 2235.2) * mm});
            skLineSegment(sketch, "E145.left", {"start": v(-12039.6, 1016) * mm, "end": v(-12039.6, 2235.2) * mm});
            skLineSegment(sketch, "E145.right", {"start": v(-10820.4, 1016) * mm, "end": v(-10820.4, 2235.2) * mm});
            skSolve(sketch);
        }
        {
            var Q0;
            Q0 = qSketchRegion(id + "F30", true);
            var Q1;
            Q1=makeQuery(id+"F6.opExtrude","SWEPT_FACE",FACE,{"disambiguationData":[OSD([sQuery(id+"F5.wireOp",EDGE,"E67.0")])]});
            extrude(context, id + "F31", {"entities" : qUnion([Q0]), "operationType" : NewBodyOperationType.REMOVE, "endBound" : BoundingType.UP_TO_SURFACE, "oppositeDirection" : true, "endBoundEntityFace" : qUnion([Q1]), "depth" : 25.4 * mm});
        }
        {
            var Q0;
            Q0=qCreatedBy(makeId("Top.planeOp"),FACE);
            var sketch = newSketch(context, id + "F32", { "sketchPlane" : qUnion([Q0])});
            skLineSegment(sketch, "E146.bottom", {"start": v(7353.3, 10985.5) * mm, "end": v(8845.55, 10985.5) * mm});
            skLineSegment(sketch, "E146.top", {"start": v(7353.3, 10261.6) * mm, "end": v(8845.55, 10261.6) * mm});
            skLineSegment(sketch, "E146.left", {"start": v(7353.3, 10985.5) * mm, "end": v(7353.3, 10261.6) * mm});
            skLineSegment(sketch, "E146.right", {"start": v(8845.55, 10985.5) * mm, "end": v(8845.55, 10261.6) * mm});
            skLineSegment(sketch, "E147.bottom", {"start": v(7378.7, 9956.8) * mm, "end": v(7556.5, 9956.8) * mm});
            skLineSegment(sketch, "E147.top", {"start": v(7378.7, 9550.4) * mm, "end": v(7556.5, 9550.4) * mm});
            skLineSegment(sketch, "E147.left", {"start": v(7378.7, 9956.8) * mm, "end": v(7378.7, 9550.4) * mm});
            skLineSegment(sketch, "E147.right", {"start": v(7556.5, 9956.8) * mm, "end": v(7556.5, 9550.4) * mm});
            skLineSegment(sketch, "E148", {"start": v(7556.5, 9753.6) * mm, "end": v(7823.2, 9753.6) * mm});
            skEllipse(sketch, "E149", {"center": v(7823.2, 9753.6) * mm, "majorRadius": 215.9 * mm, "minorRadius": 184.15 * mm, "majorAxis": v(1, 0)});
            skPoint(sketch, "E150", {"position": v(8039.1, 9753.6) * mm});
            skLineSegment(sketch, "E151.bottom", {"start": v(7353.3, 8382) * mm, "end": v(7912.1, 8382) * mm});
            skLineSegment(sketch, "E151.top", {"start": v(7353.3, 9347.2) * mm, "end": v(7912.1, 9347.2) * mm});
            skLineSegment(sketch, "E151.left", {"start": v(7353.3, 8382) * mm, "end": v(7353.3, 9347.2) * mm});
            skLineSegment(sketch, "E151.right", {"start": v(7912.1, 8382) * mm, "end": v(7912.1, 9347.2) * mm});
            skLineSegment(sketch, "E152", {"start": v(7353.3, 9347.2) * mm, "end": v(7912.1, 8382) * mm, "construction": true});
            skLineSegment(sketch, "E153", {"start": v(7353.3, 8382) * mm, "end": v(7912.1, 9347.2) * mm, "construction": true});
            skEllipse(sketch, "E154", {"center": v(7632.7, 8864.6) * mm, "majorRadius": 203.2 * mm, "minorRadius": 152.4 * mm, "majorAxis": v(0, 1), "construction": true});
            skLineSegment(sketch, "E155.bottom", {"start": v(10560.05, 10934.7) * mm, "end": v(12903.2, 10934.7) * mm});
            skLineSegment(sketch, "E155.top", {"start": v(10560.05, 10274.3) * mm, "end": v(12903.2, 10274.3) * mm});
            skLineSegment(sketch, "E155.left", {"start": v(10560.05, 10934.7) * mm, "end": v(10560.05, 10274.3) * mm});
            skLineSegment(sketch, "E155.right", {"start": v(12903.2, 10934.7) * mm, "end": v(12903.2, 10274.3) * mm});
            skLineSegment(sketch, "E156.bottom", {"start": v(12928.6, 10960.1) * mm, "end": v(13843, 10960.1) * mm});
            skLineSegment(sketch, "E156.top", {"start": v(12928.6, 10096.5) * mm, "end": v(13843, 10096.5) * mm});
            skLineSegment(sketch, "E156.left", {"start": v(12928.6, 10960.1) * mm, "end": v(12928.6, 10096.5) * mm});
            skLineSegment(sketch, "E156.right", {"start": v(13843, 10960.1) * mm, "end": v(13843, 10096.5) * mm});
            skLineSegment(sketch, "E157.bottom", {"start": v(11049, 10795) * mm, "end": v(11404.6, 10795) * mm});
            skLineSegment(sketch, "E157.top", {"start": v(11049, 10414) * mm, "end": v(11404.6, 10414) * mm});
            skLineSegment(sketch, "E157.left", {"start": v(11049, 10795) * mm, "end": v(11049, 10414) * mm});
            skLineSegment(sketch, "E157.right", {"start": v(11404.6, 10795) * mm, "end": v(11404.6, 10414) * mm});
            skLineSegment(sketch, "E158.bottom", {"start": v(11455.4, 10795) * mm, "end": v(11811, 10795) * mm});
            skLineSegment(sketch, "E158.top", {"start": v(11455.4, 10414) * mm, "end": v(11811, 10414) * mm});
            skLineSegment(sketch, "E158.left", {"start": v(11455.4, 10795) * mm, "end": v(11455.4, 10414) * mm});
            skLineSegment(sketch, "E158.right", {"start": v(11811, 10795) * mm, "end": v(11811, 10414) * mm});
            skLineSegment(sketch, "E159", {"start": v(11404.6, 10604.5) * mm, "end": v(11455.4, 10604.5) * mm, "construction": true});
            skPoint(sketch, "E160", {"position": v(11430, 10604.5) * mm});
            skLineSegment(sketch, "E161", {"start": v(11430, 10934.7) * mm, "end": v(11430, 10274.3) * mm, "construction": true});
            skLineSegment(sketch, "E162.bottom", {"start": v(8959.85, 10934.7) * mm, "end": v(9569.45, 10934.7) * mm});
            skLineSegment(sketch, "E162.top", {"start": v(8959.85, 10528.3) * mm, "end": v(9569.45, 10528.3) * mm});
            skLineSegment(sketch, "E162.left", {"start": v(8959.85, 10934.7) * mm, "end": v(8959.85, 10528.3) * mm});
            skLineSegment(sketch, "E162.right", {"start": v(9569.45, 10934.7) * mm, "end": v(9569.45, 10528.3) * mm});
            skEllipse(sketch, "E163", {"center": v(8099.43, 10623.55) * mm, "majorRadius": 609.6 * mm, "minorRadius": 279.4 * mm, "majorAxis": v(1, 0), "construction": true});
            skLineSegment(sketch, "E164", {"start": v(7353.3, 10985.5) * mm, "end": v(8845.55, 10261.6) * mm, "construction": true});
            skLineSegment(sketch, "E165", {"start": v(8845.55, 10985.5) * mm, "end": v(7353.3, 10261.6) * mm, "construction": true});
            skSolve(sketch);
        }
        {
            var Q0;
            Q0=makeQuery(id+"F8.opExtrude","SWEPT_FACE",FACE,{"disambiguationData":[OSD([sQuery(id+"F7.wireOp",EDGE,"E70")])]});
            var sketch = newSketch(context, id + "F33", { "sketchPlane" : qUnion([Q0])});
            skLineSegment(sketch, "E166.bottom", {"start": v(8458.2, 0) * mm, "end": v(9220.2, 0) * mm});
            skLineSegment(sketch, "E166.top", {"start": v(8458.2, 2082.8) * mm, "end": v(9220.2, 2082.8) * mm});
            skLineSegment(sketch, "E166.left", {"start": v(8458.2, 0) * mm, "end": v(8458.2, 2082.8) * mm});
            skLineSegment(sketch, "E166.right", {"start": v(9220.2, 0) * mm, "end": v(9220.2, 2082.8) * mm});
            skSolve(sketch);
        }
        {
            var Q0;
            Q0 = qSketchRegion(id + "F33", true);
            extrude(context, id + "F34", {"entities" : qUnion([Q0]), "operationType" : NewBodyOperationType.REMOVE, "endBound" : BoundingType.UP_TO_NEXT, "oppositeDirection" : true, "depth" : 25.4 * mm});
        }
        {
            var Q0;
            Q0=makeQuery(id+"F8.opExtrude","SWEPT_FACE",FACE,{"disambiguationData":[OSD([sQuery(id+"F7.wireOp",EDGE,"E75")])]});
            var sketch = newSketch(context, id + "F35", { "sketchPlane" : qUnion([Q0])});
            skLineSegment(sketch, "E167.bottom", {"start": v(9759.95, 0) * mm, "end": v(10369.55, 0) * mm});
            skLineSegment(sketch, "E167.top", {"start": v(9759.95, 2082.8) * mm, "end": v(10369.55, 2082.8) * mm});
            skLineSegment(sketch, "E167.left", {"start": v(9759.95, 0) * mm, "end": v(9759.95, 2082.8) * mm});
            skLineSegment(sketch, "E167.right", {"start": v(10369.55, 0) * mm, "end": v(10369.55, 2082.8) * mm});
            skSolve(sketch);
        }
        {
            var Q0;
            Q0 = qSketchRegion(id + "F35", true);
            extrude(context, id + "F36", {"entities" : qUnion([Q0]), "operationType" : NewBodyOperationType.REMOVE, "endBound" : BoundingType.UP_TO_NEXT, "oppositeDirection" : true, "depth" : 25.4 * mm});
        }
        {
            var Q0;
            Q0=makeQuery(id+"F2.opExtrude","CAP_FACE",FACE,{"disambiguationData":[OSD([sQuery(id+"F0.wireOp",EDGE,"E0.bottom"),sQuery(id+"F0.wireOp",EDGE,"E0.top"),sQuery(id+"F0.wireOp",EDGE,"E0.left"),sQuery(id+"F0.wireOp",EDGE,"E0.right"),sQuery(id+"F0.wireOp",EDGE,"E1"),sQuery(id+"F0.wireOp",EDGE,"E2"),sQuery(id+"F0.wireOp",EDGE,"E3"),sQuery(id+"F0.wireOp",EDGE,"E4"),sQuery(id+"F0.wireOp",EDGE,"E5"),sQuery(id+"F0.wireOp",EDGE,"E6"),sQuery(id+"F0.wireOp",EDGE,"E16.0"),sQuery(id+"F0.wireOp",EDGE,"E17.0"),sQuery(id+"F0.wireOp",EDGE,"E18.0"),sQuery(id+"F0.wireOp",EDGE,"E19.0"),sQuery(id+"F0.wireOp",EDGE,"E20.0"),sQuery(id+"F0.wireOp",EDGE,"E21.0"),sQuery(id+"F0.wireOp",EDGE,"E22.0"),sQuery(id+"F0.wireOp",EDGE,"E23.0"),sQuery(id+"F0.wireOp",EDGE,"E24.0"),sQuery(id+"F0.wireOp",EDGE,"E25.0")])],"isStart":false});
            var sketch = newSketch(context, id + "F37", { "sketchPlane" : qUnion([Q0])});
            skPoint(sketch, "E168", {"position": v(15836.9, 1054.1) * mm});
            skPoint(sketch, "E169", {"position": v(15836.9, 2781.3) * mm});
            skPoint(sketch, "E170", {"position": v(17995.9, 2781.3) * mm});
            skPoint(sketch, "E171", {"position": v(17995.9, 1054.1) * mm});
            skLineSegment(sketch, "E172.bottom", {"start": v(15836.9, 2781.3) * mm, "end": v(17995.9, 2781.3) * mm, "construction": true});
            skLineSegment(sketch, "E172.top", {"start": v(15836.9, 1054.1) * mm, "end": v(17995.9, 1054.1) * mm, "construction": true});
            skLineSegment(sketch, "E172.left", {"start": v(15836.9, 2781.3) * mm, "end": v(15836.9, 1054.1) * mm, "construction": true});
            skLineSegment(sketch, "E172.right", {"start": v(17995.9, 2781.3) * mm, "end": v(17995.9, 1054.1) * mm, "construction": true});
            skLineSegment(sketch, "E173.bottom", {"start": v(11010.9, 2781.3) * mm, "end": v(13169.9, 2781.3) * mm, "construction": true});
            skLineSegment(sketch, "E173.top", {"start": v(11010.9, 1054.1) * mm, "end": v(13169.9, 1054.1) * mm, "construction": true});
            skLineSegment(sketch, "E173.left", {"start": v(11010.9, 2781.3) * mm, "end": v(11010.9, 1054.1) * mm, "construction": true});
            skLineSegment(sketch, "E173.right", {"start": v(13169.9, 2781.3) * mm, "end": v(13169.9, 1054.1) * mm, "construction": true});
            skPoint(sketch, "E174", {"position": v(11010.9, 2781.3) * mm});
            skPoint(sketch, "E175", {"position": v(11010.9, 1054.1) * mm});
            skPoint(sketch, "E176", {"position": v(13169.9, 1054.1) * mm});
            skPoint(sketch, "E177", {"position": v(13169.9, 2781.3) * mm});
            skLineSegment(sketch, "E178", {"start": v(11010.9, 2781.3) * mm, "end": v(13169.9, 1054.1) * mm, "construction": true});
            skPoint(sketch, "E179", {"position": v(12090.4, 1917.7) * mm});
            skLineSegment(sketch, "E180", {"start": v(15836.9, 2781.3) * mm, "end": v(17995.9, 1054.1) * mm, "construction": true});
            skPoint(sketch, "E181", {"position": v(16916.4, 1917.7) * mm});
            skPoint(sketch, "E182", {"position": v(10064.75, 9880.6) * mm});
            skLineSegment(sketch, "E183", {"start": v(10064.75, 9880.6) * mm, "end": v(10064.75, 10185.4) * mm, "construction": true});
            skPoint(sketch, "E184", {"position": v(11430, 10629.9) * mm});
            skPoint(sketch, "E185", {"position": v(15557.5, 4273.55) * mm});
            skPoint(sketch, "E186", {"position": v(17820.22, 4273.55) * mm});
            skPoint(sketch, "E187", {"position": v(10598.15, 5722.94) * mm});
            skPoint(sketch, "E188", {"position": v(12860.87, 5722.94) * mm});
            skPoint(sketch, "E189", {"position": v(15123.58, 5722.94) * mm});
            skPoint(sketch, "E190", {"position": v(15123.58, 10071.1) * mm});
            skPoint(sketch, "E191", {"position": v(17386.3, 10071.1) * mm});
            skPoint(sketch, "E192", {"position": v(10598.15, 7172.32) * mm});
            skPoint(sketch, "E193", {"position": v(12860.87, 7172.32) * mm});
            skPoint(sketch, "E194", {"position": v(15123.58, 7172.32) * mm});
            skPoint(sketch, "E195", {"position": v(17386.3, 7172.32) * mm});
            skPoint(sketch, "E196", {"position": v(7556.5, 8864.6) * mm});
            skPoint(sketch, "E197", {"position": v(8099.43, 10623.55) * mm});
            skPoint(sketch, "E198", {"position": v(9264.65, 10172.7) * mm});
            skLineSegment(sketch, "E199", {"start": v(10598.15, 7172.32) * mm, "end": v(12860.87, 7172.32) * mm, "construction": true});
            skLineSegment(sketch, "E200", {"start": v(12860.87, 7172.32) * mm, "end": v(15123.58, 7172.32) * mm, "construction": true});
            skLineSegment(sketch, "E201", {"start": v(15123.58, 7172.32) * mm, "end": v(17386.3, 7172.32) * mm, "construction": true});
            skLineSegment(sketch, "E202", {"start": v(10598.15, 5722.94) * mm, "end": v(12860.87, 5722.94) * mm, "construction": true});
            skLineSegment(sketch, "E203", {"start": v(12860.87, 5722.94) * mm, "end": v(15123.58, 5722.94) * mm, "construction": true});
            skLineSegment(sketch, "E204", {"start": v(15123.58, 10071.1) * mm, "end": v(17386.3, 10071.1) * mm, "construction": true});
            skLineSegment(sketch, "E205", {"start": v(15557.5, 4273.55) * mm, "end": v(17820.22, 4273.55) * mm, "construction": true});
            skLineSegment(sketch, "E206", {"start": v(15123.58, 5722.94) * mm, "end": v(17386.3, 5722.94) * mm, "construction": true});
            skPoint(sketch, "E207", {"position": v(17386.3, 5722.94) * mm});
            skLineSegment(sketch, "E208", {"start": v(17386.3, 7172.32) * mm, "end": v(17386.3, 5722.94) * mm, "construction": true});
            skLineSegment(sketch, "E209", {"start": v(17386.3, 5722.94) * mm, "end": v(17386.3, 4273.55) * mm, "construction": true});
            skLineSegment(sketch, "E210", {"start": v(17820.22, 4273.55) * mm, "end": v(18910.3, 4273.55) * mm, "construction": true});
            skLineSegment(sketch, "E211", {"start": v(18910.3, 4737.1) * mm, "end": v(18910.3, 3810) * mm, "construction": true});
            skPoint(sketch, "E212", {"position": v(4330.7, 4229.1) * mm});
            skPoint(sketch, "E213", {"position": v(6699.25, 4229.1) * mm});
            skPoint(sketch, "E214", {"position": v(9067.8, 4229.1) * mm});
            skPoint(sketch, "E215", {"position": v(9067.8, 1054.1) * mm});
            skPoint(sketch, "E216", {"position": v(6699.25, 1054.1) * mm});
            skPoint(sketch, "E217", {"position": v(4330.7, 1054.1) * mm});
            skLineSegment(sketch, "E218", {"start": v(4330.7, 4229.1) * mm, "end": v(4330.7, 1054.1) * mm, "construction": true});
            skLineSegment(sketch, "E219", {"start": v(4330.7, 1054.1) * mm, "end": v(6699.25, 1054.1) * mm, "construction": true});
            skLineSegment(sketch, "E220", {"start": v(6699.25, 1054.1) * mm, "end": v(9067.8, 1054.1) * mm, "construction": true});
            skLineSegment(sketch, "E221", {"start": v(3416.3, 2641.6) * mm, "end": v(4330.7, 2641.6) * mm, "construction": true});
            skLineSegment(sketch, "E222", {"start": v(3416.3, 139.7) * mm, "end": v(9982.2, 139.7) * mm});
            skLineSegment(sketch, "E223", {"start": v(6699.25, 139.7) * mm, "end": v(6699.25, 1054.1) * mm, "construction": true});
            skPoint(sketch, "E224", {"position": v(6699.25, 2641.6) * mm});
            skPoint(sketch, "E225", {"position": v(9067.8, 2641.6) * mm});
            skPoint(sketch, "E226", {"position": v(4330.7, 2641.6) * mm});
            skPoint(sketch, "E227", {"position": v(10598.15, 8621.71) * mm});
            skPoint(sketch, "E228", {"position": v(12860.87, 8621.71) * mm});
            skPoint(sketch, "E229", {"position": v(15123.58, 8621.71) * mm});
            skPoint(sketch, "E230", {"position": v(17386.3, 8621.71) * mm});
            skLineSegment(sketch, "E231", {"start": v(17386.3, 7172.32) * mm, "end": v(17386.3, 8621.71) * mm, "construction": true});
            skLineSegment(sketch, "E232", {"start": v(17386.3, 8621.71) * mm, "end": v(17386.3, 10071.1) * mm, "construction": true});
            skLineSegment(sketch, "E233", {"start": v(10598.15, 8621.71) * mm, "end": v(12860.87, 8621.71) * mm, "construction": true});
            skLineSegment(sketch, "E234", {"start": v(12860.87, 8621.71) * mm, "end": v(15123.58, 8621.71) * mm, "construction": true});
            skLineSegment(sketch, "E235", {"start": v(15123.58, 8621.71) * mm, "end": v(17386.3, 8621.71) * mm, "construction": true});
            skPoint(sketch, "E236", {"position": v(16254.94, 10071.1) * mm});
            skSolve(sketch);
        }
    });
